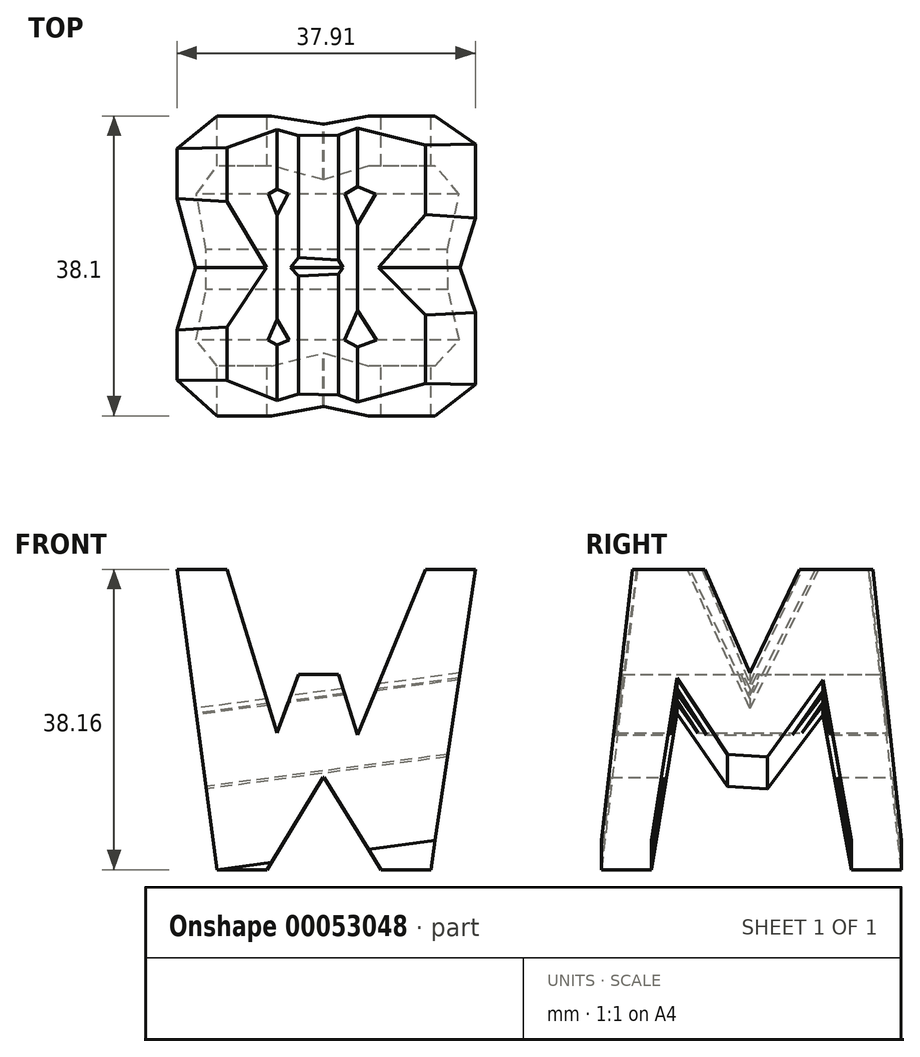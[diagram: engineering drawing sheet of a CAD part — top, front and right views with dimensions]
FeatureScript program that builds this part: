
annotation { "Feature Type Name" : "Feature", "Feature Type Description" : "" }
export const myFeature = defineFeature(function(context is Context, id is Id, definition is map)
    precondition{}
    {
        {
            var Q0;
            Q0=qCreatedBy(makeId("Front.planeOp"),FACE);
            cPlane(context, id + "F0", {"entities" : qUnion([Q0]), "cplaneType" : CPlaneType.OFFSET, "offset" : 38.1 * mm, "width" : 152.4 * mm, "height" : 152.4 * mm});
        }
        {
            var Q0;
            Q0=qCreatedBy(id+"F0.planeOp",FACE);
            var sketch = newSketch(context, id + "F1", { "sketchPlane" : qUnion([Q0])});
            skLineSegment(sketch, "E0", {"start": v(0, 0) * mm, "end": v(0, 38.16) * mm});
            skLineSegment(sketch, "E1", {"start": v(0, 38.16) * mm, "end": v(37.91, 38.16) * mm});
            skLineSegment(sketch, "E2", {"start": v(37.91, 38.16) * mm, "end": v(37.91, 0) * mm});
            skLineSegment(sketch, "E3", {"start": v(37.91, 0) * mm, "end": v(0, 0) * mm});
            skSolve(sketch);
        }
        {
            var Q0;
            Q0 = qSketchRegion(id + "F1", true);
            extrude(context, id + "F2", {"entities" : qUnion([Q0]), "oppositeDirection" : true, "depth" : 38.1 * mm});
        }
        {
            var Q0;
            Q0=makeQuery(id+"F2.opExtrude","CAP_FACE",FACE,{"disambiguationData":[OSD([sQuery(id+"F1.wireOp",EDGE,"E0"),sQuery(id+"F1.wireOp",EDGE,"E1"),sQuery(id+"F1.wireOp",EDGE,"E2"),sQuery(id+"F1.wireOp",EDGE,"E3")])],"isStart":false});
            var sketch = newSketch(context, id + "F3", { "sketchPlane" : qUnion([Q0])});
            skLineSegment(sketch, "E4", {"start": v(-37.91, 38.16) * mm, "end": v(-31.56, 38.16) * mm});
            skLineSegment(sketch, "E5", {"start": v(-31.56, 38.16) * mm, "end": v(-22.95, 17.12) * mm});
            skLineSegment(sketch, "E6", {"start": v(-22.95, 17.12) * mm, "end": v(-20.5, 24.78) * mm});
            skLineSegment(sketch, "E7", {"start": v(-20.5, 24.78) * mm, "end": v(-15.43, 24.78) * mm});
            skLineSegment(sketch, "E8", {"start": v(-15.43, 24.78) * mm, "end": v(-12.73, 17.38) * mm});
            skLineSegment(sketch, "E9", {"start": v(-12.73, 17.38) * mm, "end": v(-6.35, 38.16) * mm});
            skLineSegment(sketch, "E10", {"start": v(-6.35, 38.16) * mm, "end": v(0, 38.16) * mm});
            skLineSegment(sketch, "E11", {"start": v(0, 38.16) * mm, "end": v(-5.1, 0) * mm});
            skLineSegment(sketch, "E12", {"start": v(-5.1, 0) * mm, "end": v(-11.45, 0) * mm});
            skLineSegment(sketch, "E13", {"start": v(-11.45, 0) * mm, "end": v(-18.59, 11.7) * mm});
            skLineSegment(sketch, "E14", {"start": v(-18.59, 11.7) * mm, "end": v(-18.67, 11.7) * mm});
            skLineSegment(sketch, "E15", {"start": v(-18.67, 11.7) * mm, "end": v(-25.9, 0) * mm});
            skLineSegment(sketch, "E16", {"start": v(-25.9, 0) * mm, "end": v(-32.25, 0) * mm});
            skLineSegment(sketch, "E17", {"start": v(-32.25, 0) * mm, "end": v(-37.91, 38.16) * mm});
            skSolve(sketch);
        }
        {
            var Q0;
            {var subQ0=sQuery(id+"F3.wireOp",EDGE,"E17");Q0=makeQuery(id+"F3.imprint","IMPRINT",FACE,{"disambiguationData":[TD([[makeQuery(id+"F3.imprint","IMPRINT",EDGE,{"derivedFrom":subQ0}),1.0]])]});}
            var Q1;
            {var subQ0=sQuery(id+"F3.wireOp",EDGE,"E5");Q1=makeQuery(id+"F3.imprint","IMPRINT",FACE,{"disambiguationData":[TD([[makeQuery(id+"F3.imprint","IMPRINT",EDGE,{"derivedFrom":subQ0}),1.0]])]});}
            var Q2;
            {var subQ0=sQuery(id+"F3.wireOp",EDGE,"E13");Q2=makeQuery(id+"F3.imprint","IMPRINT",FACE,{"disambiguationData":[TD([[makeQuery(id+"F3.imprint","IMPRINT",EDGE,{"derivedFrom":subQ0}),1.0]])]});}
            var Q3;
            {var subQ0=sQuery(id+"F3.wireOp",EDGE,"E11");Q3=makeQuery(id+"F3.imprint","IMPRINT",FACE,{"disambiguationData":[TD([[makeQuery(id+"F3.imprint","IMPRINT",EDGE,{"derivedFrom":subQ0}),1.0]])]});}
            extrude(context, id + "F4", {"entities" : qUnion([Q0, Q1, Q2, Q3]), "operationType" : NewBodyOperationType.REMOVE, "oppositeDirection" : true, "depth" : 50.8 * mm});
        }
        {
            var Q0;
            Q0=makeQuery(id+"F4.boolean.opBoolean","COPY",FACE,{"derivedFrom":makeQuery(id+"F4.opExtrude","SWEPT_FACE",FACE,{"disambiguationData":[OSD([sQuery(id+"F3.wireOp",EDGE,"E11")])]})});
            var sketch = newSketch(context, id + "F5", { "sketchPlane" : qUnion([Q0])});
            skLineSegment(sketch, "E18", {"start": v(0, -0.68) * mm, "end": v(4.14, 37.82) * mm});
            skLineSegment(sketch, "E19", {"start": v(4.14, 37.82) * mm, "end": v(10.5, 37.82) * mm});
            skLineSegment(sketch, "E20", {"start": v(10.5, 37.82) * mm, "end": v(19.26, 20) * mm});
            skLineSegment(sketch, "E21", {"start": v(19.26, 20) * mm, "end": v(27.19, 37.82) * mm});
            skLineSegment(sketch, "E22", {"start": v(27.19, 37.82) * mm, "end": v(33.54, 37.82) * mm});
            skLineSegment(sketch, "E23", {"start": v(33.54, 37.82) * mm, "end": v(38.1, -0.68) * mm});
            skLineSegment(sketch, "E24", {"start": v(38.1, -0.68) * mm, "end": v(31.75, -0.68) * mm});
            skLineSegment(sketch, "E25", {"start": v(31.75, -0.68) * mm, "end": v(28.47, 19.37) * mm});
            skLineSegment(sketch, "E26", {"start": v(28.47, 19.37) * mm, "end": v(22.05, 9.97) * mm});
            skLineSegment(sketch, "E27", {"start": v(22.05, 9.97) * mm, "end": v(16.98, 9.67) * mm});
            skLineSegment(sketch, "E28", {"start": v(16.98, 9.67) * mm, "end": v(9.94, 19.16) * mm});
            skLineSegment(sketch, "E29", {"start": v(9.94, 19.16) * mm, "end": v(6.35, -0.68) * mm});
            skLineSegment(sketch, "E30", {"start": v(6.35, -0.68) * mm, "end": v(0, -0.68) * mm});
            skSolve(sketch);
        }
        {
            var Q0;
            {var subQ0=sQuery(id+"F5.wireOp",EDGE,"E20");Q0=makeQuery(id+"F5.imprint","IMPRINT",FACE,{"disambiguationData":[TD([[makeQuery(id+"F5.imprint","IMPRINT",EDGE,{"derivedFrom":subQ0}),1.0]])]});}
            var Q1;
            {var subQ0=sQuery(id+"F5.wireOp",EDGE,"E18");Q1=makeQuery(id+"F5.imprint","IMPRINT",FACE,{"disambiguationData":[TD([[makeQuery(id+"F5.imprint","IMPRINT",EDGE,{"derivedFrom":subQ0}),1.0]])]});}
            var Q2;
            {var subQ0=sQuery(id+"F5.wireOp",EDGE,"E25");Q2=makeQuery(id+"F5.imprint","IMPRINT",FACE,{"disambiguationData":[TD([[makeQuery(id+"F5.imprint","IMPRINT",EDGE,{"derivedFrom":subQ0}),1.0]])]});}
            var Q3;
            {var subQ0=sQuery(id+"F5.wireOp",EDGE,"E23");Q3=makeQuery(id+"F5.imprint","IMPRINT",FACE,{"disambiguationData":[TD([[makeQuery(id+"F5.imprint","IMPRINT",EDGE,{"derivedFrom":subQ0}),1.0]])]});}
            extrude(context, id + "F6", {"entities" : qUnion([Q0, Q1, Q2, Q3]), "operationType" : NewBodyOperationType.REMOVE, "oppositeDirection" : true, "depth" : 38.1 * mm});
        }
        {
            var Q0;
            Q0=makeQuery(id+"F6.boolean.opBoolean","COPY",FACE,{"disambiguationData":[OD(1.0)],"derivedFrom":makeQuery(id+"F6.opExtrude","SWEPT_FACE",FACE,{"disambiguationData":[OSD([sQuery(id+"F1.wireOp",EDGE,"E3"),sQuery(id+"F3.wireOp",EDGE,"E11"),sQuery(id+"F3.wireOp",EDGE,"E12")])]})});
            var Q1;
            Q1=makeQuery(id+"F6.boolean.opBoolean","COPY",FACE,{"disambiguationData":[OD(0.0)],"derivedFrom":makeQuery(id+"F6.opExtrude","SWEPT_FACE",FACE,{"disambiguationData":[OSD([sQuery(id+"F1.wireOp",EDGE,"E3"),sQuery(id+"F3.wireOp",EDGE,"E11"),sQuery(id+"F3.wireOp",EDGE,"E12")])]})});
            extrude(context, id + "F7", {"entities" : qUnion([Q0, Q1]), "operationType" : NewBodyOperationType.REMOVE, "oppositeDirection" : true, "depth" : 25.4 * mm});
        }
    });
